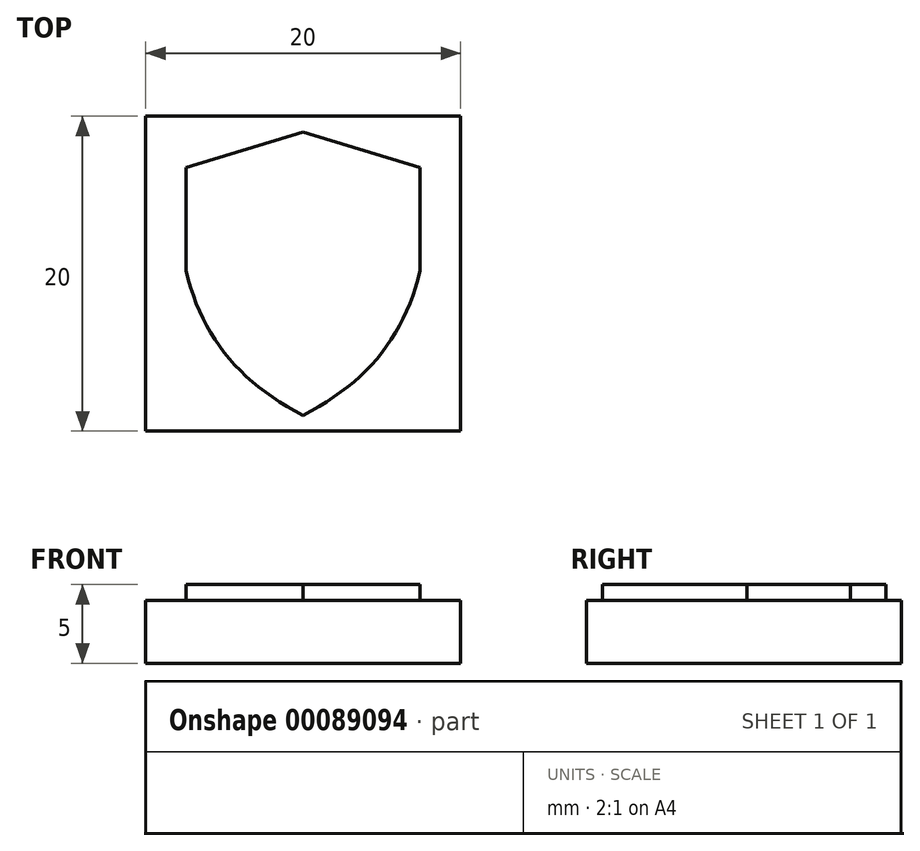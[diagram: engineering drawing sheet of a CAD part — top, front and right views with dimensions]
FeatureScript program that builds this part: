
annotation { "Feature Type Name" : "Feature", "Feature Type Description" : "" }
export const myFeature = defineFeature(function(context is Context, id is Id, definition is map)
    precondition{}
    {
        {
            var Q0;
            Q0=qCreatedBy(makeId("Top.planeOp"),FACE);
            var sketch = newSketch(context, id + "F0", { "sketchPlane" : qUnion([Q0])});
            skLineSegment(sketch, "E0.bottom", {"start": v(-50.7, 5.54) * mm, "end": v(-30.7, 5.54) * mm});
            skLineSegment(sketch, "E0.top", {"start": v(-50.7, -14.46) * mm, "end": v(-30.7, -14.46) * mm});
            skLineSegment(sketch, "E0.left", {"start": v(-50.7, 5.54) * mm, "end": v(-50.7, -14.46) * mm});
            skLineSegment(sketch, "E0.right", {"start": v(-30.7, 5.54) * mm, "end": v(-30.7, -14.46) * mm});
            skLineSegment(sketch, "E1.0", {"start": v(-49.7, 4.54) * mm, "end": v(-49.7, -13.46) * mm, "construction": true});
            skLineSegment(sketch, "E1.1", {"start": v(-49.7, 4.54) * mm, "end": v(-31.7, 4.54) * mm, "construction": true});
            skLineSegment(sketch, "E1.2", {"start": v(-31.7, 4.54) * mm, "end": v(-31.7, -13.46) * mm, "construction": true});
            skLineSegment(sketch, "E1.3", {"start": v(-49.7, -13.46) * mm, "end": v(-31.7, -13.46) * mm, "construction": true});
            skLineSegment(sketch, "E2", {"start": v(-40.7, -12.14) * mm, "end": v(-40.7, 3.26) * mm});
            skPoint(sketch, "E2.startSnap0", {"position": v(-40.7, -13.46) * mm});
            skLineSegment(sketch, "E3", {"start": v(-40.7, 3.34) * mm, "end": v(-40.7, -12.14) * mm});
            skLineSegment(sketch, "E4", {"start": v(-48.13, 2.3) * mm, "end": v(-40.7, 4.54) * mm});
            skLineSegment(sketch, "E5", {"start": v(-40.7, 3.34) * mm, "end": v(-47.08, 1.44) * mm});
            skLineSegment(sketch, "E6", {"start": v(-48.13, 2.3) * mm, "end": v(-48.13, -4.27) * mm});
            skLineSegment(sketch, "E7", {"start": v(-47.08, 1.44) * mm, "end": v(-47.08, -3.66) * mm});
            skFitSpline(sketch, "E8", {"points": [v(-48.13, -4.27) * mm, v(-40.7, -13.46) * mm], "startDerivative": vector(2.95, -12.58) * mm, "endDerivative": vector(12, -6.13) * mm});
            skLineSegment(sketch, "E9", {"start": v(-40.7, 6.64) * mm, "end": v(-40.7, -15.7) * mm, "construction": true});
            skPoint(sketch, "E9.startSnap0", {"position": v(-40.7, 5.54) * mm});
            skLineSegment(sketch, "E10.MirrorCS", {"start": v(-33.26, 2.3) * mm, "end": v(-40.7, 4.54) * mm});
            skLineSegment(sketch, "E11.MirrorCS", {"start": v(-33.26, 2.3) * mm, "end": v(-33.26, -4.27) * mm});
            skFitSpline(sketch, "E12.MirrorCS", {"points": [v(-33.26, -4.27) * mm, v(-40.7, -13.46) * mm], "startDerivative": vector(-2.95, -12.58) * mm, "endDerivative": vector(-12, -6.13) * mm});
            skFitSpline(sketch, "E13", {"points": [v(-40.7, -12.14) * mm, v(-47.08, -3.66) * mm], "startDerivative": vector(-11.23, 6.28) * mm, "endDerivative": vector(-0.2, 8.5) * mm});
            skSolve(sketch);
        }
        {
            var Q0;
            Q0=makeQuery(id+"F0.imprint","IMPRINT",FACE,{"disambiguationData":[TD([[makeQuery(id+"F0.imprint","IMPRINT",EDGE,{"derivedFrom":sQuery(id+"F0.wireOp",EDGE,"E0.bottom")}),-1.0]])]});
            extrude(context, id + "F1", {"entities" : qUnion([Q0]), "depth" : 4 * mm});
        }
        {
            var Q0;
            Q0=makeQuery(id+"F0.imprint","IMPRINT",FACE,{"disambiguationData":[TD([[makeQuery(id+"F0.imprint","IMPRINT",EDGE,{"derivedFrom":sQuery(id+"F0.wireOp",EDGE,"E4")}),-1.0]])]});
            extrude(context, id + "F2", {"entities" : qUnion([Q0]), "operationType" : NewBodyOperationType.ADD, "depth" : 5 * mm});
        }
        {
            var Q0;
            {var subQ0=sQuery(id+"F0.wireOp",EDGE,"E5");Q0=makeQuery(id+"F0.imprint","IMPRINT",FACE,{"disambiguationData":[TD([[makeQuery(id+"F0.imprint","IMPRINT",EDGE,{"derivedFrom":subQ0}),1.0]])]});}
            extrude(context, id + "F3", {"entities" : qUnion([Q0]), "operationType" : NewBodyOperationType.ADD, "depth" : 5 * mm});
        }
    });
